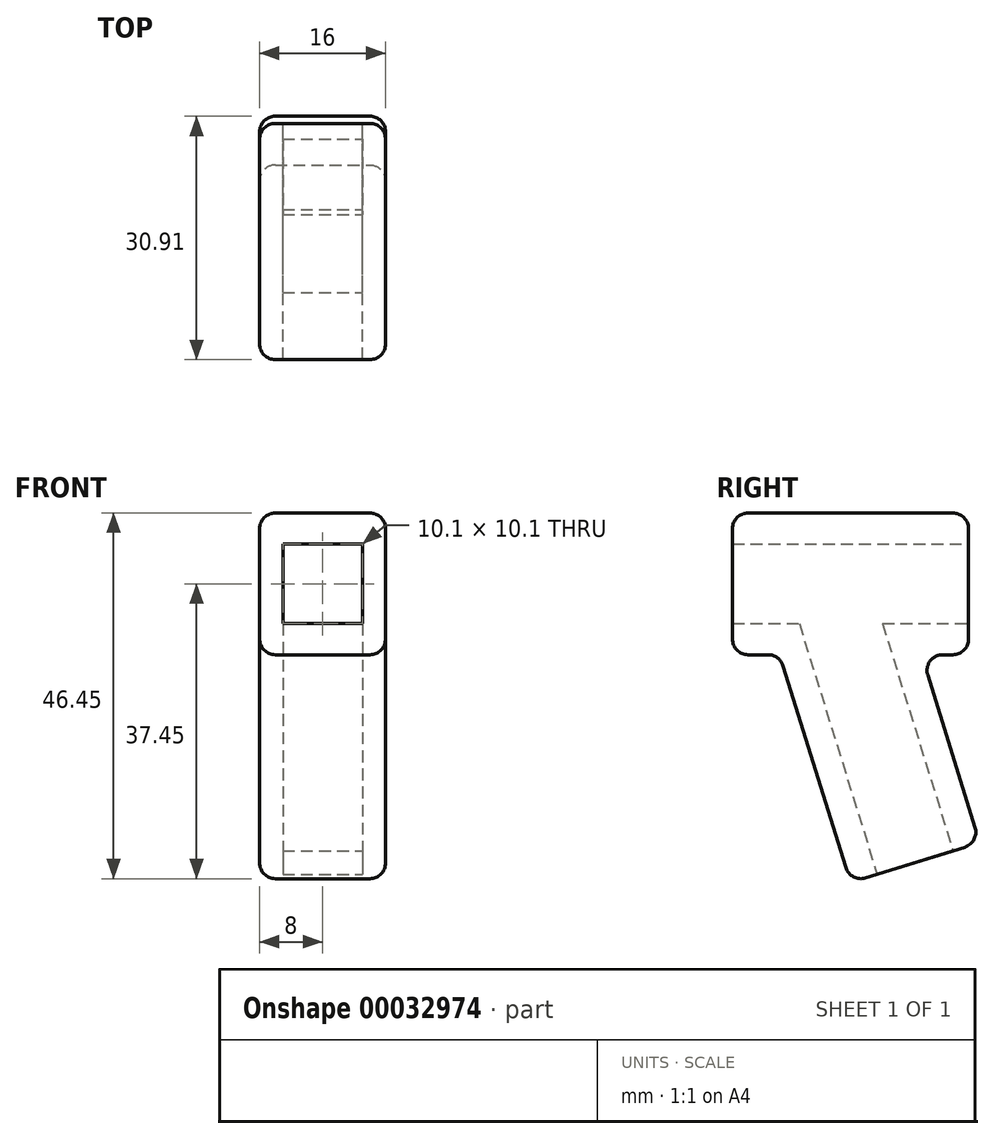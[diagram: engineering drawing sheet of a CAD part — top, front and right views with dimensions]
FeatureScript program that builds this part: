
annotation { "Feature Type Name" : "Feature", "Feature Type Description" : "" }
export const myFeature = defineFeature(function(context is Context, id is Id, definition is map)
    precondition{}
    {
        {
            var Q0;
            Q0=qCreatedBy(makeId("Right.planeOp"),FACE);
            var sketch = newSketch(context, id + "F0", { "sketchPlane" : qUnion([Q0])});
            skLineSegment(sketch, "E0.rect.bottom", {"start": v(15, -9) * mm, "end": v(9, -9) * mm});
            skLineSegment(sketch, "E0.rect.top", {"start": v(15, 9) * mm, "end": v(-15, 9) * mm});
            skLineSegment(sketch, "E0.rect.left", {"start": v(15, -9) * mm, "end": v(15, 9) * mm});
            skLineSegment(sketch, "E0.rect.right", {"start": v(-15, -9) * mm, "end": v(-15, 9) * mm});
            skPoint(sketch, "E0.rect.middle", {"position": v(0, 0) * mm});
            skLineSegment(sketch, "E1.rect.bottom", {"start": v(9, -9) * mm, "end": v(-9, -9) * mm, "construction": true});
            skLineSegment(sketch, "E1.rect.top", {"start": v(9, 9) * mm, "end": v(-9, 9) * mm, "construction": true});
            skLineSegment(sketch, "E1.rect.left", {"start": v(9, -9) * mm, "end": v(9, 9) * mm, "construction": true});
            skLineSegment(sketch, "E1.rect.right", {"start": v(-9, -9) * mm, "end": v(-9, 9) * mm, "construction": true});
            skLineSegment(sketch, "E2", {"start": v(-9, -9) * mm, "end": v(0, -37.95) * mm});
            skLineSegment(sketch, "E3", {"start": v(9, -9) * mm, "end": v(16.41, -32.85) * mm});
            skLineSegment(sketch, "E4.trimOffspring", {"start": v(-9, -9) * mm, "end": v(-15, -9) * mm});
            skLineSegment(sketch, "E5", {"start": v(0, -37.95) * mm, "end": v(16.41, -32.85) * mm});
            skPoint(sketch, "E6.orphan", {"position": v(18, -37.95) * mm});
            skSolve(sketch);
        }
        {
            var Q0;
            Q0=qSketchRegion(id+"F0",true);
            extrude(context, id + "F1", {"entities" : qUnion([Q0]), "depth" : 16 * mm, "symmetric" : true});
        }
        {
            var Q0;
            Q0=makeQuery(id+"F1.opExtrude","SWEPT_FACE",FACE,{"disambiguationData":[OSD([sQuery(id+"F0.wireOp",EDGE,"E0.rect.left")])]});
            var sketch = newSketch(context, id + "F2", { "sketchPlane" : qUnion([Q0])});
            skLineSegment(sketch, "E7.rect.bottom", {"start": v(5.05, -5.05) * mm, "end": v(-5.05, -5.05) * mm});
            skLineSegment(sketch, "E7.rect.top", {"start": v(5.05, 5.05) * mm, "end": v(-5.05, 5.05) * mm});
            skLineSegment(sketch, "E7.rect.left", {"start": v(5.05, -5.05) * mm, "end": v(5.05, 5.05) * mm});
            skLineSegment(sketch, "E7.rect.right", {"start": v(-5.05, -5.05) * mm, "end": v(-5.05, 5.05) * mm});
            skPoint(sketch, "E7.rect.middle", {"position": v(0, 0) * mm});
            skSolve(sketch);
        }
        {
            var Q0;
            Q0=qSketchRegion(id+"F2",true);
            extrude(context, id + "F3", {"entities" : qUnion([Q0]), "operationType" : NewBodyOperationType.REMOVE, "endBound" : BoundingType.UP_TO_NEXT, "oppositeDirection" : true, "depth" : 25 * mm});
        }
        {
            var Q0;
            Q0=makeQuery(id+"F1.opExtrude","SWEPT_FACE",FACE,{"disambiguationData":[OSD([sQuery(id+"F0.wireOp",EDGE,"E5")])]});
            var sketch = newSketch(context, id + "F4", { "sketchPlane" : qUnion([Q0])});
            skLineSegment(sketch, "E8", {"start": v(8, 11.27) * mm, "end": v(-8, -5.92) * mm, "construction": true});
            skLineSegment(sketch, "E9", {"start": v(-8, -5.92) * mm, "end": v(8, -5.92) * mm, "construction": true});
            skLineSegment(sketch, "E10", {"start": v(8, -5.92) * mm, "end": v(-8, 11.27) * mm, "construction": true});
            skLineSegment(sketch, "E11.rect.bottom", {"start": v(-5.05, -2.38) * mm, "end": v(5.05, -2.38) * mm});
            skLineSegment(sketch, "E11.rect.top", {"start": v(-5.05, 7.72) * mm, "end": v(5.05, 7.72) * mm});
            skLineSegment(sketch, "E11.rect.left", {"start": v(-5.05, -2.38) * mm, "end": v(-5.05, 7.72) * mm});
            skLineSegment(sketch, "E11.rect.right", {"start": v(5.05, -2.38) * mm, "end": v(5.05, 7.72) * mm});
            skPoint(sketch, "E11.rect.middle", {"position": v(0, 2.67) * mm});
            skSolve(sketch);
        }
        {
            var Q0;
            Q0=qSketchRegion(id+"F4",true);
            extrude(context, id + "F5", {"entities" : qUnion([Q0]), "operationType" : NewBodyOperationType.REMOVE, "endBound" : BoundingType.UP_TO_NEXT, "oppositeDirection" : true, "depth" : 25 * mm});
        }
        {
            var Q0;
            Q0=makeQuery(id+"F1.opExtrude","SWEPT_FACE",FACE,{"disambiguationData":[OSD([sQuery(id+"F0.wireOp",EDGE,"E0.rect.top")])]});
            var Q1;
            Q1=makeQuery(id+"F1.opExtrude","CAP_FACE",FACE,{"disambiguationData":[OSD([sQuery(id+"F0.wireOp",EDGE,"E0.rect.bottom"),sQuery(id+"F0.wireOp",EDGE,"E0.rect.top"),sQuery(id+"F0.wireOp",EDGE,"E0.rect.left"),sQuery(id+"F0.wireOp",EDGE,"E0.rect.right"),sQuery(id+"F0.wireOp",EDGE,"E2"),sQuery(id+"F0.wireOp",EDGE,"E3"),sQuery(id+"F0.wireOp",EDGE,"E4.trimOffspring"),sQuery(id+"F0.wireOp",EDGE,"E5")])],"isStart":true});
            var Q2;
            Q2=makeQuery(id+"F1.opExtrude","SWEPT_FACE",FACE,{"disambiguationData":[OSD([sQuery(id+"F0.wireOp",EDGE,"E2")])]});
            var Q3;
            Q3=makeQuery(id+"F1.opExtrude","CAP_FACE",FACE,{"disambiguationData":[OSD([sQuery(id+"F0.wireOp",EDGE,"E0.rect.bottom"),sQuery(id+"F0.wireOp",EDGE,"E0.rect.top"),sQuery(id+"F0.wireOp",EDGE,"E0.rect.left"),sQuery(id+"F0.wireOp",EDGE,"E0.rect.right"),sQuery(id+"F0.wireOp",EDGE,"E2"),sQuery(id+"F0.wireOp",EDGE,"E3"),sQuery(id+"F0.wireOp",EDGE,"E4.trimOffspring"),sQuery(id+"F0.wireOp",EDGE,"E5")])],"isStart":false});
            var Q4;
            Q4=makeQuery(id+"F1.opExtrude","SWEPT_FACE",FACE,{"disambiguationData":[OSD([sQuery(id+"F0.wireOp",EDGE,"E3")])]});
            var Q5;
            Q5=makeQuery(id+"F1.opExtrude","SWEPT_FACE",FACE,{"disambiguationData":[OSD([sQuery(id+"F0.wireOp",EDGE,"E0.rect.bottom")])]});
            var Q6;
            Q6=makeQuery(id+"F1.opExtrude","SWEPT_FACE",FACE,{"disambiguationData":[OSD([sQuery(id+"F0.wireOp",EDGE,"E4.trimOffspring")])]});
            fillet(context, id + "F6", {"entities" : qUnion([Q0, Q1, Q2, Q3, Q4, Q5, Q6]), "radius" : 2 * mm, "tangentPropagation" : true, "allowEdgeOverflow" : false});
        }
    });
